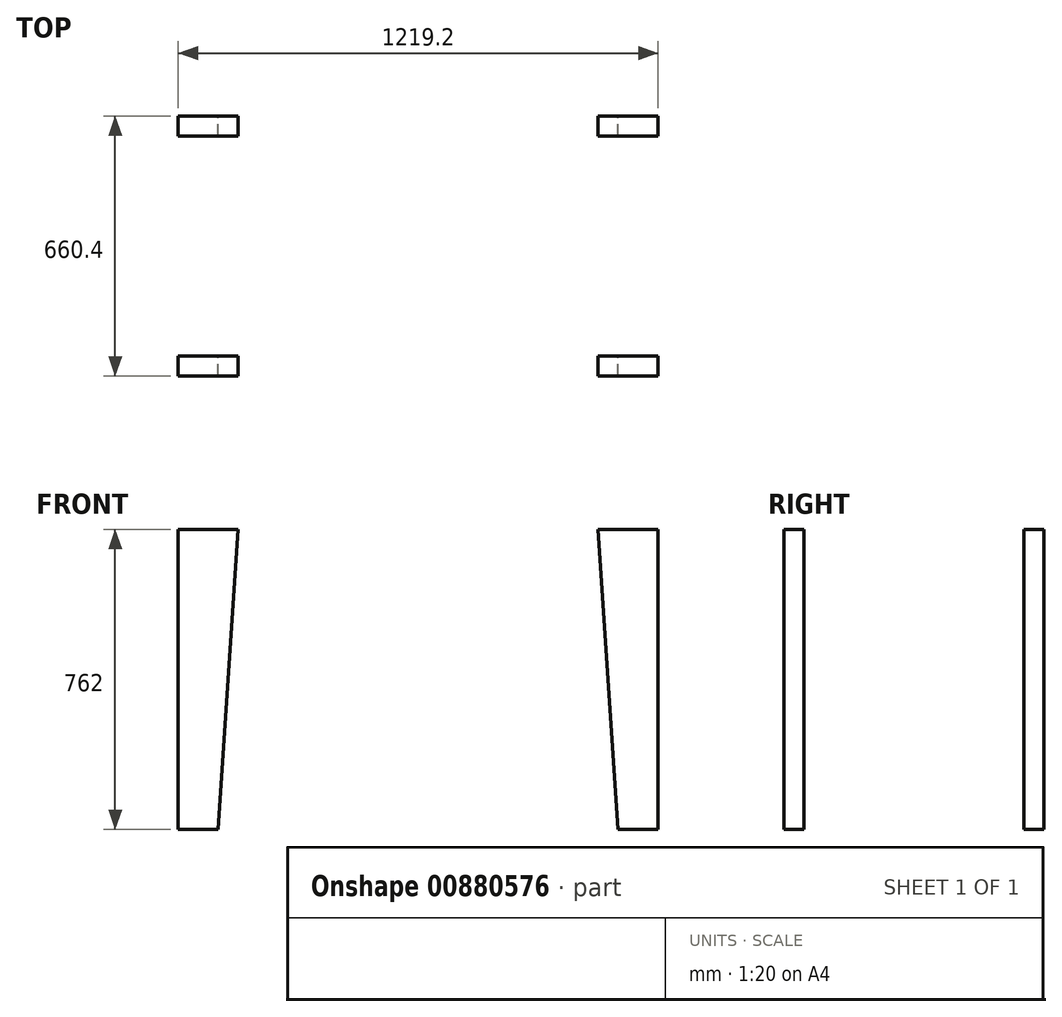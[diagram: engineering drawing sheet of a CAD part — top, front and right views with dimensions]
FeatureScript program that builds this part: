
annotation { "Feature Type Name" : "Feature", "Feature Type Description" : "" }
export const myFeature = defineFeature(function(context is Context, id is Id, definition is map)
    precondition{}
    {
        {
            var Q0;
            Q0=qCreatedBy(makeId("Front.planeOp"),FACE);
            var sketch = newSketch(context, id + "F0", { "sketchPlane" : qUnion([Q0])});
            skLineSegment(sketch, "E0", {"start": v(-82.06, 710.55) * mm, "end": v(-82.06, -51.45) * mm});
            skLineSegment(sketch, "E1", {"start": v(-82.06, -51.45) * mm, "end": v(19.54, -51.45) * mm});
            skLineSegment(sketch, "E2", {"start": v(-82.06, 710.55) * mm, "end": v(70.34, 710.55) * mm});
            skLineSegment(sketch, "E3", {"start": v(70.34, 710.55) * mm, "end": v(19.54, -51.45) * mm});
            skSolve(sketch);
        }
        {
            var Q0;
            Q0 = qSketchRegion(id + "F0", true);
            extrude(context, id + "F1", {"entities" : qUnion([Q0]), "depth" : 50.8 * mm, "offsetDistance" : 25.4 * mm});
        }
        {
            var Q0;
            Q0=makeQuery(id+"F1.opExtrude","SWEPT_BODY",BODY,{"disambiguationData":[OSD([sQuery(id+"F0.wireOp",EDGE,"E0"),sQuery(id+"F0.wireOp",EDGE,"E1"),sQuery(id+"F0.wireOp",EDGE,"E2"),sQuery(id+"F0.wireOp",EDGE,"E3")])]});
            transform(context, id + "F2", {"entities" : qUnion([Q0]), "transformType" : TransformType.TRANSLATION_3D, "dx" : 0 * mm, "dy" : 609.6 * mm, "dz" : 0 * mm, "makeCopy" : true});
        }
        {
            var Q0;
            Q0=makeQuery(id+"F2.opPattern","COPY",BODY,{"derivedFrom":makeQuery(id+"F1.opExtrude","SWEPT_BODY",BODY,{"disambiguationData":[OSD([sQuery(id+"F0.wireOp",EDGE,"E0"),sQuery(id+"F0.wireOp",EDGE,"E1"),sQuery(id+"F0.wireOp",EDGE,"E2"),sQuery(id+"F0.wireOp",EDGE,"E3")])]}),"instanceName":"1"});
            transform(context, id + "F3", {"entities" : qUnion([Q0]), "transformType" : TransformType.TRANSLATION_3D, "dx" : 1219.2 * mm, "dy" : 0 * mm, "dz" : 0 * mm, "makeCopy" : true});
        }
        {
            var Q0;
            Q0=makeQuery(id+"F3.opPattern","COPY",BODY,{"derivedFrom":makeQuery(id+"F2.opPattern","COPY",BODY,{"derivedFrom":makeQuery(id+"F1.opExtrude","SWEPT_BODY",BODY,{"disambiguationData":[OSD([sQuery(id+"F0.wireOp",EDGE,"E0"),sQuery(id+"F0.wireOp",EDGE,"E1"),sQuery(id+"F0.wireOp",EDGE,"E2"),sQuery(id+"F0.wireOp",EDGE,"E3")])]}),"instanceName":"1"}),"instanceName":"1"});
            var Q1;
            Q1=makeQuery(id+"F3.opPattern","COPY",FACE,{"derivedFrom":makeQuery(id+"F2.opPattern","COPY",FACE,{"derivedFrom":makeQuery(id+"F1.opExtrude","SWEPT_FACE",FACE,{"disambiguationData":[OSD([sQuery(id+"F0.wireOp",EDGE,"E0")])]}),"instanceName":"1"}),"instanceName":"1"});
            mirror(context, id + "F4", {"entities" : qUnion([Q0]), "mirrorPlane" : qUnion([Q1])});
        }
        {
            var Q0;
            Q0=makeQuery(id+"F3.opPattern","COPY",BODY,{"derivedFrom":makeQuery(id+"F2.opPattern","COPY",BODY,{"derivedFrom":makeQuery(id+"F1.opExtrude","SWEPT_BODY",BODY,{"disambiguationData":[OSD([sQuery(id+"F0.wireOp",EDGE,"E0"),sQuery(id+"F0.wireOp",EDGE,"E1"),sQuery(id+"F0.wireOp",EDGE,"E2"),sQuery(id+"F0.wireOp",EDGE,"E3")])]}),"instanceName":"1"}),"instanceName":"1"});
            deleteBodies(context, id + "F5", {"entities" : qUnion([Q0])});
        }
        {
            var Q0;
            Q0=makeQuery(id+"F4.opPattern","COPY",BODY,{"derivedFrom":makeQuery(id+"F3.opPattern","COPY",BODY,{"derivedFrom":makeQuery(id+"F2.opPattern","COPY",BODY,{"derivedFrom":makeQuery(id+"F1.opExtrude","SWEPT_BODY",BODY,{"disambiguationData":[OSD([sQuery(id+"F0.wireOp",EDGE,"E0"),sQuery(id+"F0.wireOp",EDGE,"E1"),sQuery(id+"F0.wireOp",EDGE,"E2"),sQuery(id+"F0.wireOp",EDGE,"E3")])]}),"instanceName":"1"}),"instanceName":"1"}),"instanceName":"1"});
            transform(context, id + "F6", {"entities" : qUnion([Q0]), "transformType" : TransformType.TRANSLATION_3D, "dx" : 0 * mm, "dy" : -609.6 * mm, "dz" : 0 * mm, "makeCopy" : true});
        }
    });
